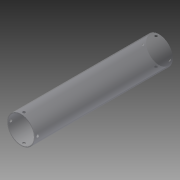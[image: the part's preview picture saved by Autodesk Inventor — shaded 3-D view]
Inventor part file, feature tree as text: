
AUTODESK INVENTOR PART (.ipt)
format: ipt  version: 2014 (Build 180170000, 170)  size: 150,528 bytes
history: native  units: in
note: dims shown in document units (in); Inventor stores cm internally (conversion verified against a paired STEP export)
features: extrude x3, sketch x3, plane x2, projected_geometry x1
ambient origin geometry x8: Origin, YZ Plane, XZ Plane, XY Plane, X Axis, Y Axis, Z Axis, Center Point
bodies: Solid1 (feature_tree)
feature tree (9):
  extrude  "Extrusion1"  Depth=1.875in
  plane  "Work Plane1"
  extrude  "Extrusion2"  Depth=5.0in
  plane  "Work Plane2"
  extrude  "Extrusion3"  Depth=0.2188in
  sketch  "Sketch1"  dims[d0=2.0in d1=1.875in]
  sketch  "Sketch2"  dims[d2=10.0in d3=0.0in d4=5.0in]
  projected_geometry  "Projected Loop1"
  sketch  "Sketch3"  dims[d5=0.19in d6=0.2188in d7=1.0in d8=2.0in d9=0.0in d10=5.0in d11=0.19in d12=0.2188in d13=1.0in d14=2.0in d15=0.0in]
